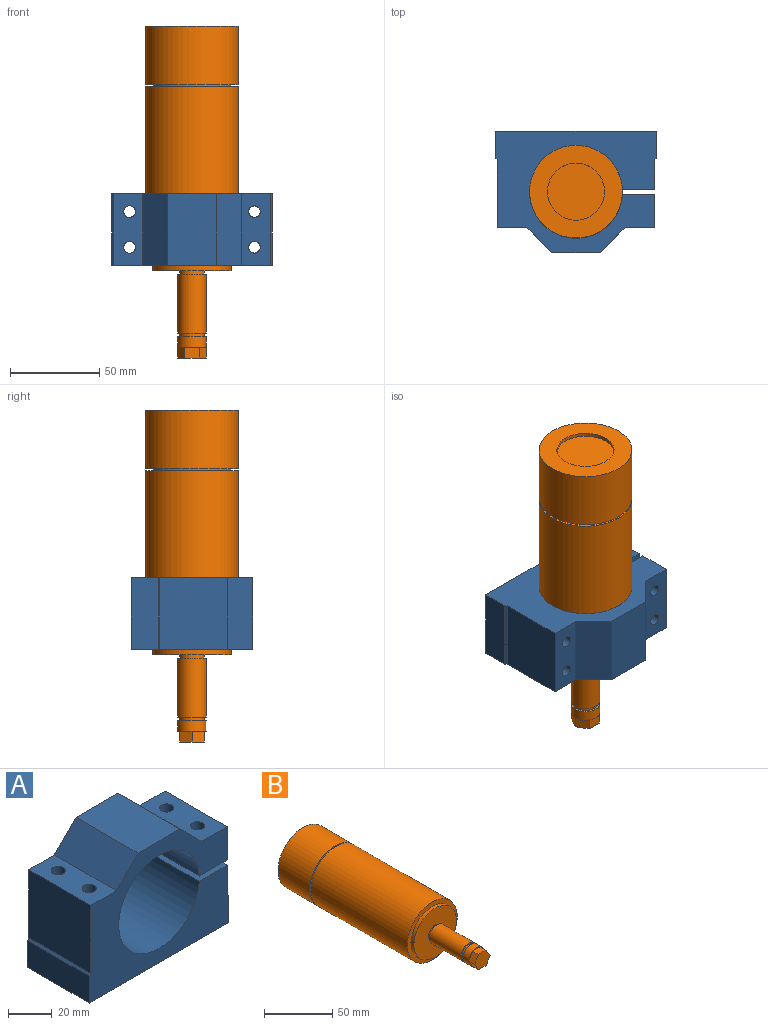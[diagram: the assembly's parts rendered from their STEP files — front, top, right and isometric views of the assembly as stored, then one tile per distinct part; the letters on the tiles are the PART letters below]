
ASSEMBLY  parts=2 mates=1
PART A: 24 faces, bbox 90x40x68 mm
  f0: plane 90x68mm, normal (0,1,0), area 3179.2mm2, adj f1,f2,f3,f4,f5,f6,f7,f8
  f1: plane 40x18.04mm, normal (0,0,-1), area 655.4mm2, adj f0,f2,f16,f17,f22,f23
  f2: plane 40x18.5mm, normal (1,0,0), area 740mm2, adj f0,f1,f3,f17
  f3: plane 40x16.5mm, normal (0,0,1), area 593.6mm2, adj f0,f2,f4,f17,f22,f23
  f4: plane 40x14mm, normal (0.71,0,0.71), area 792mm2, adj f0,f3,f5,f17
  f5: plane 40x27mm, normal (0,0,1), area 1080mm2, adj f0,f4,f6,f17
  f6: plane 40x14mm, normal (-0.71,0,0.71), area 792mm2, adj f0,f5,f7,f17
  f7: plane 40x16.5mm, normal (0,0,1), area 593.6mm2, adj f0,f6,f8,f17,f20,f21
  f8: plane 40x38mm, normal (-1,0,0), area 1520mm2, adj f0,f7,f9,f17
  f9: plane 40x1mm, normal (-0.71,0,0.71), area 56.6mm2, adj f0,f8,f10,f17
  f10: plane 40x15mm, normal (-1,0,0), area 600mm2, adj f0,f9,f11,f17
  f11: plane 90x40mm, normal (0,0,-1), area 3467.3mm2, adj f0,f10,f12,f17,f18,f19,f20,f21
  f12: plane 40x15mm, normal (1,0,0), area 600mm2, adj f0,f11,f13,f17
  f13: plane 40x1mm, normal (0.71,0,0.71), area 56.6mm2, adj f0,f12,f14,f17
  f14: plane 40x16.5mm, normal (1,0,0), area 660mm2, adj f0,f13,f15,f17
  f15: plane 40x18.04mm, normal (0,0,1), area 655.4mm2, adj f0,f14,f16,f17,f18,f19
  f16: cylinder r=26mm len=52mm, axis (0,-1,0), area 6414.4mm2, adj f0,f1,f15,f17
  f17: plane 90x68mm, normal (0,-1,0), area 3179.2mm2, adj f1,f2,f3,f4,f5,f6,f7,f8
  f18: cylinder r=3.25mm len=32.5mm, axis (0,0,1), area 663.7mm2, adj f11,f15
  f19: cylinder r=3.25mm len=32.5mm, axis (0,0,1), area 663.7mm2, adj f11,f15
  f20: cylinder r=3.25mm len=54mm, axis (0,0,1), area 1102.7mm2, adj f7,f11
  f21: cylinder r=3.25mm len=54mm, axis (0,0,1), area 1102.7mm2, adj f7,f11
  f22: cylinder r=3.25mm len=18.5mm, axis (0,0,1), area 377.8mm2, adj f1,f3
  f23: cylinder r=3.25mm len=18.5mm, axis (0,0,1), area 377.8mm2, adj f1,f3
PART B: 31 faces, bbox 52x186x52 mm
  f0: cylinder r=8mm len=16mm, axis (0,-1,0), area 301.6mm2, adj f3,f18,f19,f20,f21,f22,f23
  f1: cylinder r=16mm len=32mm, axis (0,-1,0), area 201.1mm2, adj f2,f17
  f2: plane 32x32mm, normal (0,1,0), area 804.2mm2, adj f1
  f3: plane 16x16mm, normal (0,1,0), area 47.1mm2, adj f0,f4
  f4: cylinder r=7mm len=14mm, axis (0,-1,0), area 88mm2, adj f3,f5
  f5: plane 16x16mm, normal (0,-1,0), area 47.1mm2, adj f4,f6
  f6: cylinder r=8mm len=33mm, axis (0,-1,0), area 1658.8mm2, adj f5,f7
  f7: plane 16x16mm, normal (0,1,0), area 47.1mm2, adj f6,f8
  f8: cylinder r=7mm len=14mm, axis (0,-1,0), area 88mm2, adj f7,f9
  f9: plane 44x44mm, normal (0,-1,0), area 1366.6mm2, adj f8,f10
  f10: cylinder r=22mm len=44mm, axis (0,-1,0), area 414.7mm2, adj f9,f11
  f11: plane 52x52mm, normal (0,-1,0), area 603.2mm2, adj f10,f12
  f12: cylinder r=26mm len=100mm, axis (0,-1,0), area 16336.3mm2, adj f11,f13
  f13: plane 52x52mm, normal (0,1,0), area 603.2mm2, adj f12,f14
  f14: cylinder r=22mm len=44mm, axis (0,-1,0), area 138.2mm2, adj f13,f15
  f15: plane 52x52mm, normal (0,-1,0), area 603.2mm2, adj f14,f16
  f16: cylinder r=26mm len=52mm, axis (0,-1,0), area 5391mm2, adj f15,f17
  f17: plane 52x52mm, normal (0,1,0), area 1319.5mm2, adj f1,f16
  f18: plane 6.93x4mm, normal (0,-1,0), area 5.8mm2, adj f0,f25
  f19: plane 6.93x4mm, normal (0,-1,0), area 5.8mm2, adj f0,f24
  f20: plane 8x1.07mm, normal (0,-1,0), area 5.8mm2, adj f0,f29
  f21: plane 6.93x4mm, normal (0,-1,0), area 5.8mm2, adj f0,f28
  f22: plane 6.93x4mm, normal (0,-1,0), area 5.8mm2, adj f0,f27
  f23: plane 8x1.07mm, normal (0,-1,0), area 5.8mm2, adj f0,f26
  f24: plane 6.93x6mm, normal (0.87,0,0.5), area 48mm2, adj f19,f25,f29,f30
  f25: plane 6.93x6mm, normal (0.87,0,-0.5), area 48mm2, adj f18,f24,f26,f30
  f26: plane 8x6mm, normal (0,0,-1), area 48mm2, adj f23,f25,f27,f30
  f27: plane 6.93x6mm, normal (-0.87,0,-0.5), area 48mm2, adj f22,f26,f28,f30
  f28: plane 6.93x6mm, normal (-0.87,0,0.5), area 48mm2, adj f21,f27,f29,f30
  f29: plane 8x6mm, normal (0,0,1), area 48mm2, adj f20,f24,f28,f30
  f30: plane 16x13.86mm, normal (0,-1,0), area 166.3mm2, adj f24,f25,f26,f27,f28,f29
PLACE A rot(axis=(1,0,0),90deg) t=(-100.2,1,0)mm
PLACE B rot(axis=(1,0,0),90deg) t=(-0.2,1,0)mm
MATE fastened B.f0 <-> A.f16  axis (0,0,-1) through (-0.2,1,0)mm
